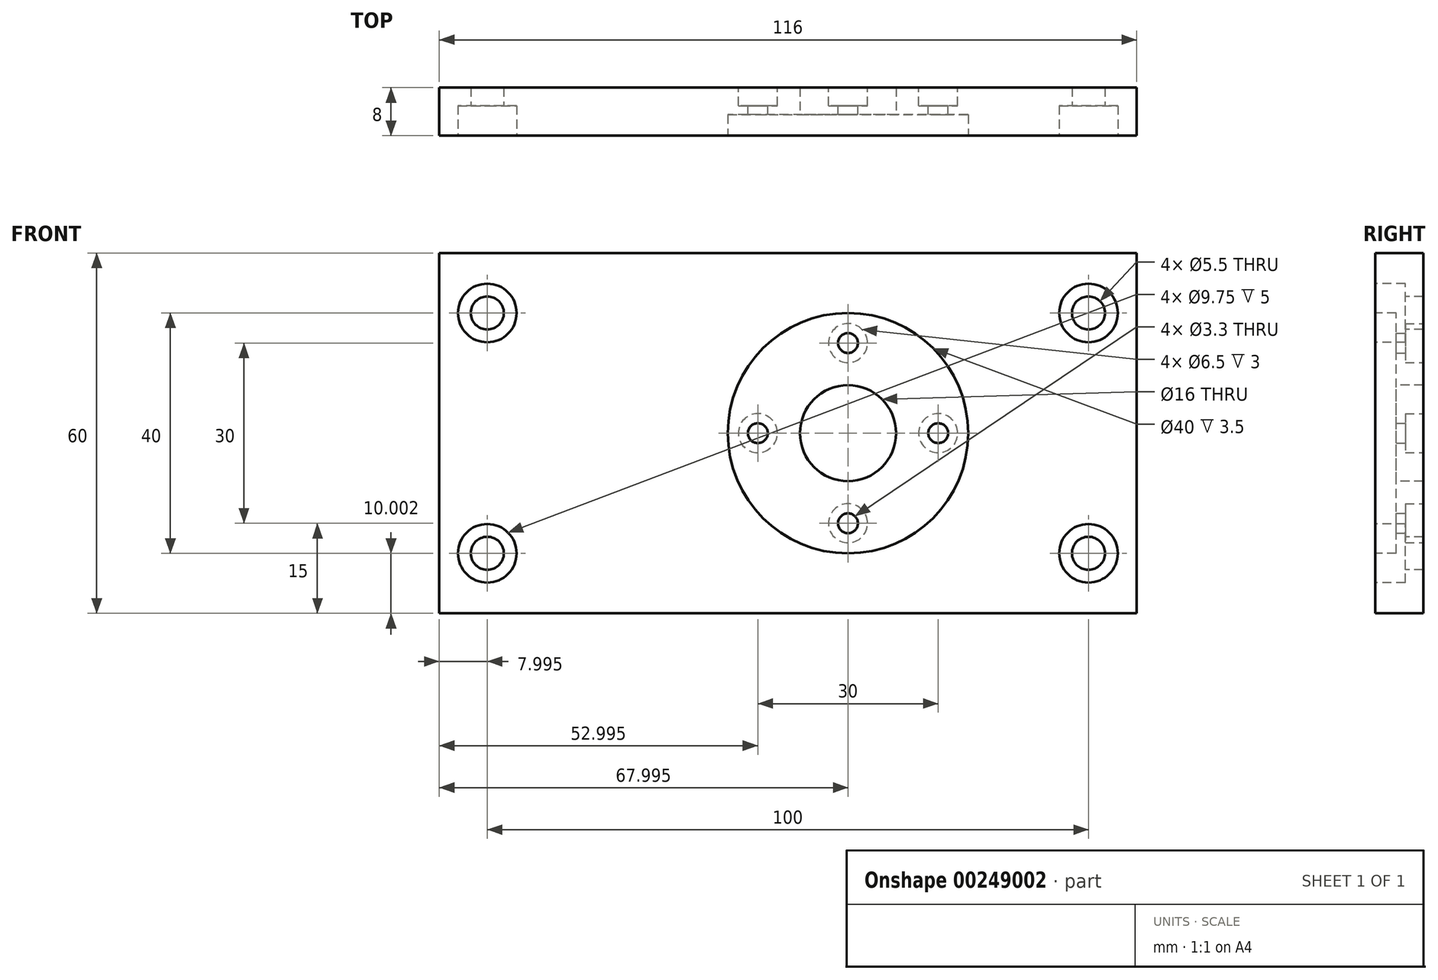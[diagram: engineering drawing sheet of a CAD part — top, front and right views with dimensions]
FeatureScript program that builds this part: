
annotation { "Feature Type Name" : "Feature", "Feature Type Description" : "" }
export const myFeature = defineFeature(function(context is Context, id is Id, definition is map)
    precondition{}
    {
        {
            var Q0;
            Q0=qCreatedBy(makeId("Front.planeOp"),FACE);
            var sketch = newSketch(context, id + "F0", { "sketchPlane" : qUnion([Q0])});
            skLineSegment(sketch, "E0.bottom", {"start": v(59.84, 30) * mm, "end": v(-56.16, 30) * mm});
            skLineSegment(sketch, "E0.top", {"start": v(59.84, -30) * mm, "end": v(-56.16, -30) * mm});
            skLineSegment(sketch, "E0.left", {"start": v(59.84, 30) * mm, "end": v(59.84, -30) * mm});
            skLineSegment(sketch, "E0.right", {"start": v(-56.16, 30) * mm, "end": v(-56.16, -30) * mm});
            skPoint(sketch, "E1", {"position": v(-48.16, 20) * mm});
            skPoint(sketch, "E2", {"position": v(-48.16, -20) * mm});
            skPoint(sketch, "E3", {"position": v(51.84, -20) * mm});
            skPoint(sketch, "E4", {"position": v(51.84, 20) * mm});
            skPoint(sketch, "E5", {"position": v(11.84, 0) * mm});
            skPoint(sketch, "E6", {"position": v(11.84, 15) * mm});
            skPoint(sketch, "E7", {"position": v(11.84, -15) * mm});
            skPoint(sketch, "E8", {"position": v(26.84, 0) * mm});
            skPoint(sketch, "E9", {"position": v(-3.16, 0) * mm});
            skSolve(sketch);
        }
        {
            var Q0;
            Q0=makeQuery(id+"F0.imprint","IMPRINT",FACE,{"disambiguationData":[TD([[makeQuery(id+"F0.imprint","IMPRINT",EDGE,{"derivedFrom":sQuery(id+"F0.wireOp",EDGE,"E0.bottom")}),1.0]])]});
            extrude(context, id + "F1", {"entities" : qUnion([Q0]), "depth" : 8 * mm});
        }
        {
            var Q0;
            Q0=makeQuery(id+"F1.opExtrude","CAP_FACE",FACE,{"disambiguationData":[OSD([sQuery(id+"F0.wireOp",EDGE,"E0.bottom"),sQuery(id+"F0.wireOp",EDGE,"E0.top"),sQuery(id+"F0.wireOp",EDGE,"E0.left"),sQuery(id+"F0.wireOp",EDGE,"E0.right")])],"isStart":false});
            var sketch = newSketch(context, id + "F2", { "sketchPlane" : qUnion([Q0])});
            skPoint(sketch, "E10.0", {"position": v(-48.16, 20) * mm});
            skPoint(sketch, "E11.0", {"position": v(-48.16, -20) * mm});
            skPoint(sketch, "E12.0", {"position": v(0, 0) * mm});
            skPoint(sketch, "E13.0", {"position": v(51.84, -20) * mm});
            skPoint(sketch, "E14.0", {"position": v(51.84, 20) * mm});
            skPoint(sketch, "E15", {"position": v(3.84, 0) * mm});
            skPoint(sketch, "E16.0", {"position": v(11.84, 0) * mm});
            skLineSegment(sketch, "E17.0.0", {"start": v(-56.16, -30) * mm, "end": v(59.84, -30) * mm});
            skLineSegment(sketch, "E17.0.1", {"start": v(59.84, -30) * mm, "end": v(59.84, 30) * mm});
            skLineSegment(sketch, "E17.0.2", {"start": v(59.84, 30) * mm, "end": v(-56.16, 30) * mm});
            skLineSegment(sketch, "E17.0.3", {"start": v(-56.16, 30) * mm, "end": v(-56.16, -30) * mm});
            skSolve(sketch);
        }
        {
            var Q0;
            Q0=sQuery(id+"F2.wireOp",VERTEX,"E10.0");
            var Q1;
            Q1=sQuery(id+"F2.wireOp",VERTEX,"E11.0");
            var Q2;
            Q2=sQuery(id+"F2.wireOp",VERTEX,"E14.0");
            var Q3;
            Q3=sQuery(id+"F2.wireOp",VERTEX,"E13.0");
            var Q4;
            Q4=makeQuery(id+"F1.opExtrude","SWEPT_BODY",BODY,{"disambiguationData":[OSD([sQuery(id+"F0.wireOp",EDGE,"E0.bottom"),sQuery(id+"F0.wireOp",EDGE,"E0.top"),sQuery(id+"F0.wireOp",EDGE,"E0.left"),sQuery(id+"F0.wireOp",EDGE,"E0.right")])]});
            hole(context, id + "F3", {"style" : HoleStyle.C_BORE, "endStyle" : HoleEndStyle.BLIND, "standardTappedOrClearance" : lookupTablePath({ "standard" : "ISO", "fit" : "Normal", "size" : "M5", "type" : "Clearance" }), "standardBlindInLast" : lookupTablePath({ "fit" : "Standard", "standard" : "ISO", "size" : "M5", "type" : "Clearance" }), "holeDiameter" : 5.5 * mm, "cBoreDiameter" : 9.75 * mm, "cBoreDepth" : 5 * mm, "holeDepth" : 13.8 * mm, "tappedDepth" : 12 * mm, "tapClearance" : 3, "startFromSketch" : true, "locations" : qUnion([Q0, Q1, Q2, Q3]), "scope" : qUnion([Q4])});
        }
        {
            var Q0;
            Q0=sQuery(id+"F2.wireOp",VERTEX,"E16.0");
            var Q1;
            Q1=makeQuery(id+"F1.opExtrude","SWEPT_BODY",BODY,{"disambiguationData":[OSD([sQuery(id+"F0.wireOp",EDGE,"E0.bottom"),sQuery(id+"F0.wireOp",EDGE,"E0.top"),sQuery(id+"F0.wireOp",EDGE,"E0.left"),sQuery(id+"F0.wireOp",EDGE,"E0.right")])]});
            hole(context, id + "F4", {"style" : HoleStyle.C_BORE, "endStyle" : HoleEndStyle.BLIND, "holeDiameter" : 16 * mm, "cBoreDiameter" : 40 * mm, "cBoreDepth" : 3.5 * mm, "holeDepth" : 13.8 * mm, "tappedDepth" : 12 * mm, "tapClearance" : 3, "startFromSketch" : true, "locations" : qUnion([Q0]), "scope" : qUnion([Q1])});
        }
        {
            var Q0;
            Q0=sQuery(id+"F0.wireOp",VERTEX,"E6");
            var Q1;
            Q1=sQuery(id+"F0.wireOp",VERTEX,"E8");
            var Q2;
            Q2=sQuery(id+"F0.wireOp",VERTEX,"E7");
            var Q3;
            Q3=sQuery(id+"F0.wireOp",VERTEX,"E9");
            var Q4;
            Q4=makeQuery(id+"F1.opExtrude","SWEPT_BODY",BODY,{"disambiguationData":[OSD([sQuery(id+"F0.wireOp",EDGE,"E0.bottom"),sQuery(id+"F0.wireOp",EDGE,"E0.top"),sQuery(id+"F0.wireOp",EDGE,"E0.left"),sQuery(id+"F0.wireOp",EDGE,"E0.right")])]});
            hole(context, id + "F5", {"style" : HoleStyle.C_BORE, "endStyle" : HoleEndStyle.BLIND, "oppositeDirection" : true, "standardTappedOrClearance" : lookupTablePath({ "standard" : "ISO", "fit" : "Normal", "size" : "M3", "type" : "Clearance" }), "standardBlindInLast" : lookupTablePath({ "fit" : "Standard", "standard" : "ISO", "size" : "M3", "type" : "Clearance" }), "holeDiameter" : 3.3 * mm, "cBoreDiameter" : 6.5 * mm, "cBoreDepth" : 3 * mm, "holeDepth" : 13.8 * mm, "tappedDepth" : 12 * mm, "tapClearance" : 3, "startFromSketch" : true, "locations" : qUnion([Q0, Q1, Q2, Q3]), "scope" : qUnion([Q4])});
        }
    });
